# Revit family: PRD_FrankeWS_WtrSpplFttngsFrWshBsnsAndTrghs_ElectronicThermostaticMixer_F5ET1016-1021
name_source: partatom
category: Plumbing Fixtures
revit_build: Autodesk Revit 2018 (Build: 20190510_1515(x64)
units: mm (PartAtom-declared; Revit-internal decimal feet)

## family parameters
Cut with Voids When Loaded = No
Host = Face
OmniClass Number = 23.45.55.17
OmniClass Title = Mixing Faucets
Part Type = Normal
Room Calculation Point = No
Round Connector Dimension = Use Diameter
Shared = No

## types (6) — shared parameters
AdjustableFlowTime = yes
AssetType = Fixed
Category = Pr_40_20_87_98, Washbasin taps
Color = Chrome
Default Elevation = 850 mm  [stored 2.78871 ft]
DefaultAutomaticHygieneFlushing = 24h after the last activity
DefaultFlowTime = 10.00 seconds
Depressurised = no
DiameterNominal = 15.000 mm
DurationUnit = year
FaucetFunction = MIXED
FaucetOperation = SELFCLOSING
FaucetType = BIB
Features = For sanitary facilities. For connection to hot and cold water.
Finish = high-polished chromium-plated brass
FlowColdWater = 0.1 L/s
FlowHotWater = 0.1 L/s
FunctionalPrinciple = electronic self-closing
HygieneFlushing = yes
IfcExportAs = IfcValveType
IfcExportType = FAUCET
InletSize = G-1-2-B
Manufacturer = KWC Group AG
ManufacturerName = KWC Group AG
ManufacturerURL = www.kwc.com
Material = Brass
MaterialsBody = Brass
MaximumFlowTime = 255.00 seconds
MinimumFlowPressure = 1.00 bar
MinimumFlowTime = 1.00 seconds
NBSDescription = Water supply fittings for wash basins and troughs
NBSReference = 45-35-70/371
NominalWidth = 305 mm  [stored 1.00066 ft]
OutletMaterial = PRD_AR_SyntheticGrey
PowerConsumption = 1.5
ProductInformation = https://pim.kwc.com
ProtectiveShutdown = yes
ProtectiveSystemIP = IP59K
SensorMaterial = PRD_AR_SyntheticDarkGrey
SoundInsulation = no
TapBottomOffset = 95 mm  [stored 0.31168 ft]
TapMaterial = PRD_AR_ChromatedBrass_HighPolished
ThermalDisinfection = automatic thermal disinfection installed
TypeOfMixing = with thermostat
TypeOfMounting = Wall mounting
TypeOfOperation = sensor operation
TypeOfSensor = opto-electronic sensor
TypeOfTap = bib tap
URL = www.kwc.com
Uniclass2015Code = Pr_40_20_87_98
Uniclass2015Title = Washbasin taps
Uniclass2015Version = Products v1.10
Version = 1
VolumeFlowRate = 0.10 L/s at 3 bar
VolumeFlowRateBypass = 0.05 liter per second
WarrantyDurationUnit = year
zero-valued in all types: NominalHeight, NominalLength

## per-type parameters (varying)
| type | BIMObjectName | Description | GrossWeight | LengthToSpout | Model | ModelNumber | ModelReference | Name | NetWeight | PositionOfPowerConnection | PowerSupplyConnection | SpoutProjection |
| F5ET1016 - 0.10 L/s with 6 V lithium battery, projection 155 mm | PRD_AR_WaterSupplyFittingsForWashBasinsAndTroughs_ElectronicThermostaticMixer_F5ET1016 | F5E-Therm thermostatic mixer DN 15 for wall mounting with lockable swivelling spout, for sanitary facilities. Opto-electronically controlled, triggered via hand movement. Thermostat with metal handle with adjustable and turn-proof temperature stop. With option for thermal disinfection, manually or automatically via pre-assembled disinfection unit. For connection to hot and cold water. Control electronics, solenoid valve cartridge, 6 V lithium battery (CR-P2) and sensor in scald-protected safe-touch housing, high-polished chromium-plated brass. Laminar jet controller with integrated flow regulator 6.0 l/min. With adjustable and lockable connections with backflow preventer and strainers, completely covered with depth-adjustable screw rosettes. Projection 155 mm. Activated water hygiene flushing 24 hours after last activation, safety switch-off with continuous reflection and saving of statistical data. With option for parameterization and communication via optional, bidirectional remote control. | 5.55 kg | 155 mm  [stored 0.50853 ft] | F5ET1016 | 2030039527 | F5ET1016 | F5 electronic thermostatic mixer F5ET1016 | 5.27 kg |  | Battery 6 V | 155.00 mm |
| F5ET1017 - 0.10 L/s with 6 V lithium battery, projection 215 mm | PRD_AR_WaterSupplyFittingsForWashBasinsAndTroughs_ElectronicThermostaticMixer_F5ET1017 | F5E-Therm thermostatic mixer DN 15 for wall mounting with lockable swivelling spout, for sanitary facilities. Opto-electronically controlled, triggered via hand movement. Thermostat with metal handle with adjustable and turn-proof temperature stop. With option for thermal disinfection, manually or automatically via pre-assembled disinfection unit. For connection to hot and cold water. Control electronics, solenoid valve cartridge, 6 V lithium battery (CR-P2) and sensor in scald-protected safe-touch housing, high-polished chromium-plated brass. Laminar jet controller with integrated flow regulator 6.0 l/min. With adjustable and lockable connections with backflow preventer and strainers, completely covered with depth-adjustable screw rosettes. Projection 215 mm. Activated water hygiene flushing 24 hours after last activation, safety switch-off with continuous reflection and saving of statistical data. With option for parameterization and communication via optional, bidirectional remote control. | 5.55 kg | 215 mm | F5ET1017 | 2030039528 | F5ET1017 | F5 electronic thermostatic mixer F5ET1017 | 5.27 kg |  | Battery 6 V | 215.00 mm |
| F5ET1018 - 0.10 L/s with 6 V lithium battery, projection 275 mm | PRD_AR_WaterSupplyFittingsForWashBasinsAndTroughs_ElectronicThermostaticMixer_F5ET1018 | F5E-Therm thermostatic mixer DN 15 for wall mounting with lockable swivelling spout, for sanitary facilities. Opto-electronically controlled, triggered via hand movement. Thermostat with metal handle with adjustable and turn-proof temperature stop. With option for thermal disinfection, manually or automatically via pre-assembled disinfection unit. For connection to hot and cold water. Control electronics, solenoid valve cartridge, 6 V lithium battery (CR-P2) and sensor in scald-protected safe-touch housing, high-polished chromium-plated brass. Laminar jet controller with integrated flow regulator 6.0 l/min. With adjustable and lockable connections with backflow preventer and strainers, completely covered with depth-adjustable screw rosettes. Projection 275 mm. Activated water hygiene flushing 24 hours after last activation, safety switch-off with continuous reflection and saving of statistical data. With option for parameterization and communication via optional, bidirectional remote control. | 5.55 kg | 275 mm | F5ET1018 | 2030039529 | F5ET1018 | F5 electronic thermostatic mixer F5ET1018 | 5.27 kg |  | Battery 6 V | 275.00 mm |
| F5ET1019 - 0.10 L/s with separate power supply via power supply unit 6.75 V / 12 V DC, projection 155 mm | PRD_AR_WaterSupplyFittingsForWashBasinsAndTroughs_ElectronicThermostaticMixer_F5ET1019 | F5E-Therm thermostatic mixer DN 15 for wall mounting with lockable swivelling spout, for sanitary facilities. Opto-electronically controlled, triggered via hand movement. Thermostat with metal handle with adjustable and turn-proof temperature stop. With option for thermal disinfection, manually or automatically via pre-assembled disinfection unit. For connection to hot and cold water. Control electronics, solenoid valve cartridge and sensor in scald-protected safe-touch housing, high-polished chromium-plated brass. Laminar jet controller with integrated flow regulator 6.0 l/min. With adjustable and lockable connections with backflow preventer and strainers, completely covered with depth-adjustable screw rosettes. Projection 155 mm. Activated water hygiene flushing 24 hours after last activation, safety switch-off with continuous reflection and saving of statistical data. With option for parameterization and communication via optional, bidirectional remote control. Separate power supply via power supply unit 6.75 V / 12 V DC or AQUA 3000 open system accessories. | 5.65 kg | 155 mm  [stored 0.50853 ft] | F5ET1019 | 2030039530 | F5ET1019 | F5 electronic thermostatic mixer F5ET1019 | 5.37 kg | from backside | 6,75 / 12 V DC / A3000 open | 155.00 mm |
| F5ET1020 - 0.10 L/s with separate power supply via power supply unit 6.75 V / 12 V DC, projection 215 mm | PRD_AR_WaterSupplyFittingsForWashBasinsAndTroughs_ElectronicThermostaticMixer_F5ET1020 | F5E-Therm thermostatic mixer DN 15 for wall mounting with lockable swivelling spout, for sanitary facilities. Opto-electronically controlled, triggered via hand movement. Thermostat with metal handle with adjustable and turn-proof temperature stop. With option for thermal disinfection, manually or automatically via pre-assembled disinfection unit. For connection to hot and cold water. Control electronics, solenoid valve cartridge and sensor in scald-protected safe-touch housing, high-polished chromium-plated brass. Laminar jet controller with integrated flow regulator 6.0 l/min. With adjustable and lockable connections with backflow preventer and strainers, completely covered with depth-adjustable screw rosettes. Projection 215 mm. Activated water hygiene flushing 24 hours after last activation, safety switch-off with continuous reflection and saving of statistical data. With option for parameterization and communication via optional, bidirectional remote control. Separate power supply via power supply unit 6.75 V / 12 V DC or AQUA 3000 open system accessories. | 5.20 kg | 215 mm | F5ET1020 | 2030039538 | F5ET1020 | F5 electronic thermostatic mixer F5ET1020 | 4.90 kg | from backside | 6,75 / 12 V DC / A3000 open | 215.00 mm |
| F5ET1021 - 0.10 L/s with separate power supply via power supply unit 6.75 V / 12 V DC, projection 275 mm | PRD_AR_WaterSupplyFittingsForWashBasinsAndTroughs_ElectronicThermostaticMixer_F5ET1021 | F5E-Therm thermostatic mixer DN 15 for wall mounting with lockable swivelling spout, for sanitary facilities. Opto-electronically controlled, triggered via hand movement. Thermostat with metal handle with adjustable and turn-proof temperature stop. With option for thermal disinfection, manually or automatically via pre-assembled disinfection unit. For connection to hot and cold water. Control electronics, solenoid valve cartridge and sensor in scald-protected safe-touch housing, high-polished chromium-plated brass. Laminar jet controller with integrated flow regulator 6.0 l/min. With adjustable and lockable connections with backflow preventer and strainers, completely covered with depth-adjustable screw rosettes. Projection 275 mm. Activated water hygiene flushing 24 hours after last activation, safety switch-off with continuous reflection and saving of statistical data. With option for parameterization and communication via optional, bidirectional remote control. Separate power supply via power supply unit 6.75 V / 12 V DC or AQUA 3000 open system accessories. | 5.65 kg | 275 mm | F5ET1021 | 2030039539 | F5ET1021 | F5 electronic thermostatic mixer F5ET1021 | 5.37 kg | from backside | 6,75 / 12 V DC / A3000 open | 275.00 mm |

note: [stored X ft] marks values corroborated as IEEE doubles in the binary element streams (Revit-internal decimal feet)

## geometry (parser evidence)
native form markers: Sweep x4
no freeform markers — native parametric forms only
